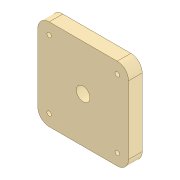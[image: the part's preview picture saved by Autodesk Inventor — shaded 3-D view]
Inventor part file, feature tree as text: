
AUTODESK INVENTOR PART (.ipt)
format: ipt  version: 2020 (Build 240168000, 168)  size: 109,056 bytes
history: native  units: mm
features: other x5, extrude x1
ambient origin geometry x8: Origin, YZ Plane, XZ Plane, XY Plane, X Axis, Y Axis, Z Axis, Center Point
bodies: Body1 (feature_tree)
feature tree (6):
  other  "Sólido1"
  other  "Plano de trabalho1"
  extrude  "Extrusão1"  Depth=12.0mm
  other  "<userpath>\OneDrive\Área de Trabalho\Calorimetro 2022\Inventor\parte_superior.iam"
  other  "parte_superior.iam"
  other  "Corpo_1:4"
